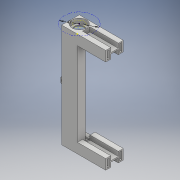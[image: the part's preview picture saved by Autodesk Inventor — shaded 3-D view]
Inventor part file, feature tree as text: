
AUTODESK INVENTOR PART (.ipt)
format: ipt  version: 2018 (Build 220112000, 112)  size: 534,528 bytes
history: native  units: mm
features: sketch x14, extrude x13, fillet x4
ambient origin geometry x8: Origin, YZ Plane, XZ Plane, XY Plane, X Axis, Y Axis, Z Axis, Center Point
bodies: Solid1 (feature_tree)
feature tree (31):
  extrude  "Extrusion1"  Depth=165.0mm
  extrude  "Extrusion2"  Depth=8.5mm
  extrude  "Extrusion3"  Depth=25.0mm TaperAngle=0.0deg
  extrude  "Extrusion4"  Depth=22.75mm
  extrude  "Extrusion5"  Depth=7.1mm
  extrude  "Extrusion6"  Depth=7.1mm TaperAngle=0.0deg
  fillet  "Fillet1"  Radius=5.0mm
  extrude  "Extrusion7"  Depth=10.0mm TaperAngle=0.0deg
  fillet  "Fillet2"  Radius=2.0mm
  extrude  "Extrusion8"  Depth=8.0mm
  extrude  "Extrusion9"  Depth=16.0mm
  fillet  "Fillet3"  Radius=8.0mm
  extrude  "Extrusion10"  Depth=6.0mm
  extrude  "Extrusion11"  Depth=3.5mm
  fillet  "Fillet4"  Radius=12.25mm
  sketch  "Sketch12"  dims[d33=3.5mm d34=12.25mm]
  extrude  "Extrusion12"  Depth=12.25mm
  extrude  "Extrusion13"  Depth=3.5mm
  sketch  "Sketch1"  dims[d0=25.0mm d1=165.0mm]
  sketch  "Sketch2"  dims[d2=3.0mm d3=0.0mm d4=8.5mm]
  sketch  "Sketch3"  dims[d5=8.5mm d6=25.0mm d7=0.0mm]
  sketch  "Sketch4"  dims[d8=25.0mm d9=22.75mm]
  sketch  "Sketch5"  dims[d10=7.1mm d11=0.0mm d12=15.5mm]
  sketch  "Sketch6"  dims[d13=165.0mm d14=0.0mm d15=7.1mm d16=0.0mm d17=5.0mm]
  sketch  "Sketch7"  dims[d18=5.0mm d19=10.0mm d20=0.0mm d21=2.0mm]
  sketch  "Sketch8"  dims[d22=16.0mm d23=8.0mm]
  sketch  "Sketch9"  dims[d24=16.0mm d25=16.0mm d26=8.0mm]
  sketch  "Sketch10"  dims[d27=45.0mm d28=0.0mm d29=6.0mm]
  sketch  "Sketch11"  dims[d30=12.25mm d31=3.5mm d32=12.25mm]
  sketch  "Sketch13"  dims[d35=12.25mm d36=3.5mm]
  sketch  "Sketch14"  dims[d37=40.0mm d38=0.0mm d39=1.0mm d40=2.0mm d41=8.0mm d42=1.0mm d43=2.0mm d44=12.0mm d45=0.0mm d46=6.0mm d47=6.0mm d48=4.0mm d49=8.0mm d50=6.5mm d51=0.0mm d52=6.35mm d53=8.0mm d54=0.0mm d55=6.5mm d56=47.0mm d57=1.0mm d58=7.0mm d59=0.0mm d60=7.1mm d61=0.0mm]
